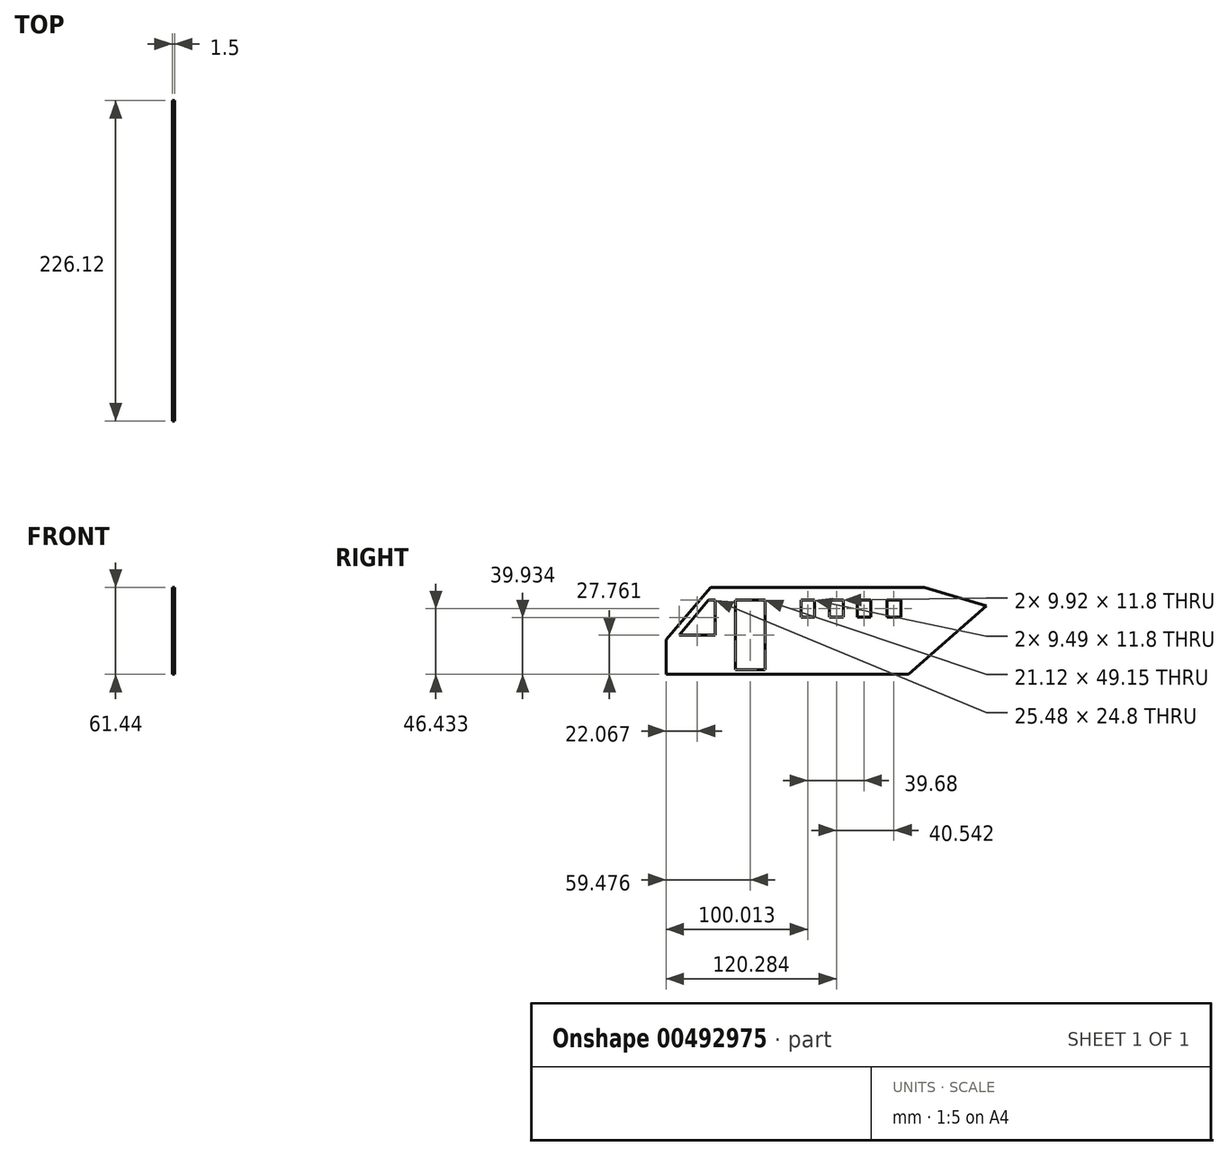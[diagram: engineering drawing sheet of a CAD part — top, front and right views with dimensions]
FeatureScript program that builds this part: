
annotation { "Feature Type Name" : "Feature", "Feature Type Description" : "" }
export const myFeature = defineFeature(function(context is Context, id is Id, definition is map)
    precondition{}
    {
        {
            var Q0;
            Q0=qCreatedBy(makeId("Right.planeOp"),FACE);
            var sketch = newSketch(context, id + "F0", { "sketchPlane" : qUnion([Q0])});
            skLineSegment(sketch, "E0", {"start": v(-80.23, -33.97) * mm, "end": v(90.94, -33.97) * mm});
            skLineSegment(sketch, "E1", {"start": v(90.94, -33.97) * mm, "end": v(145.9, 14.25) * mm});
            skLineSegment(sketch, "E2", {"start": v(145.9, 14.25) * mm, "end": v(102.1, 27.47) * mm});
            skLineSegment(sketch, "E3", {"start": v(102.1, 27.47) * mm, "end": v(-48.83, 27.47) * mm});
            skLineSegment(sketch, "E4", {"start": v(-80.23, -33.97) * mm, "end": v(-80.23, -9.4) * mm});
            skLineSegment(sketch, "E5", {"start": v(-80.23, -9.4) * mm, "end": v(-48.83, 27.47) * mm});
            skSolve(sketch);
        }
        {
            var Q0;
            Q0 = qSketchRegion(id + "F0", true);
            extrude(context, id + "F1", {"entities" : qUnion([Q0]), "depth" : 1.5 * mm});
        }
        {
            var Q0;
            Q0=makeQuery(id+"F1.opExtrude","CAP_FACE",FACE,{"disambiguationData":[OSD([sQuery(id+"F0.wireOp",EDGE,"E0"),sQuery(id+"F0.wireOp",EDGE,"E1"),sQuery(id+"F0.wireOp",EDGE,"E2"),sQuery(id+"F0.wireOp",EDGE,"E3"),sQuery(id+"F0.wireOp",EDGE,"E4"),sQuery(id+"F0.wireOp",EDGE,"E5")])],"isStart":false});
            var sketch = newSketch(context, id + "F2", { "sketchPlane" : qUnion([Q0])});
            skLineSegment(sketch, "E6", {"start": v(-70.9, -6.44) * mm, "end": v(-45.42, -6.44) * mm});
            skLineSegment(sketch, "E7", {"start": v(-70.9, -6.44) * mm, "end": v(-50.2, 18.36) * mm});
            skLineSegment(sketch, "E8", {"start": v(-45.42, -6.44) * mm, "end": v(-45.42, 18.36) * mm});
            skLineSegment(sketch, "E9", {"start": v(-45.42, 18.36) * mm, "end": v(-50.2, 18.36) * mm});
            skLineSegment(sketch, "E10", {"start": v(-31.31, 18.36) * mm, "end": v(-31.31, -30.78) * mm});
            skPoint(sketch, "E10.startSnap0", {"position": v(-47.81, 18.36) * mm});
            skLineSegment(sketch, "E11", {"start": v(-31.31, -30.78) * mm, "end": v(-10.2, -30.78) * mm});
            skLineSegment(sketch, "E12", {"start": v(-10.2, -30.78) * mm, "end": v(-10.2, 18.36) * mm});
            skLineSegment(sketch, "E13", {"start": v(-10.2, 18.36) * mm, "end": v(-31.31, 18.36) * mm});
            skLineSegment(sketch, "E14", {"start": v(15.04, 18.36) * mm, "end": v(24.53, 18.36) * mm});
            skLineSegment(sketch, "E15", {"start": v(35.1, 18.36) * mm, "end": v(45.01, 18.36) * mm});
            skLineSegment(sketch, "E16", {"start": v(54.72, 18.36) * mm, "end": v(64.2, 18.36) * mm});
            skLineSegment(sketch, "E17", {"start": v(75.64, 18.36) * mm, "end": v(85.56, 18.36) * mm});
            skLineSegment(sketch, "E18", {"start": v(85.56, 18.36) * mm, "end": v(85.56, 6.56) * mm});
            skLineSegment(sketch, "E19", {"start": v(75.64, 18.36) * mm, "end": v(75.64, 6.56) * mm});
            skLineSegment(sketch, "E20", {"start": v(64.2, 18.36) * mm, "end": v(64.2, 6.56) * mm});
            skLineSegment(sketch, "E21", {"start": v(54.72, 18.36) * mm, "end": v(54.72, 6.56) * mm});
            skLineSegment(sketch, "E22", {"start": v(15.04, 18.36) * mm, "end": v(15.04, 6.56) * mm});
            skLineSegment(sketch, "E23", {"start": v(24.53, 18.36) * mm, "end": v(24.53, 6.56) * mm});
            skLineSegment(sketch, "E24", {"start": v(35.1, 18.36) * mm, "end": v(35.1, 6.56) * mm});
            skLineSegment(sketch, "E25", {"start": v(45.01, 18.36) * mm, "end": v(45.01, 6.56) * mm});
            skLineSegment(sketch, "E26", {"start": v(15.04, 6.56) * mm, "end": v(24.53, 6.56) * mm});
            skLineSegment(sketch, "E27", {"start": v(35.1, 6.56) * mm, "end": v(45.01, 6.56) * mm});
            skLineSegment(sketch, "E28", {"start": v(54.72, 6.56) * mm, "end": v(64.2, 6.56) * mm});
            skLineSegment(sketch, "E29", {"start": v(75.64, 6.56) * mm, "end": v(85.56, 6.56) * mm});
            skSolve(sketch);
        }
        {
            var Q0;
            Q0 = qSketchRegion(id + "F2", true);
            extrude(context, id + "F3", {"entities" : qUnion([Q0]), "operationType" : NewBodyOperationType.REMOVE, "oppositeDirection" : true, "depth" : 1.5 * mm});
        }
    });
